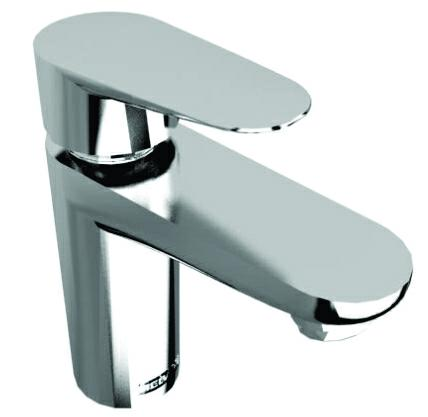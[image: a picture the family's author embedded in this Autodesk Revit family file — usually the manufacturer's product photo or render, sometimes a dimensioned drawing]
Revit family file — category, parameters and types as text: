
# Revit family: Monomando de Lavabo E-928
name_source: partatom
category: Aparatos sanitarios
revit_build: Autodesk Revit 2016 (Build: 20150220_1215(x64)
units: mm (PartAtom-declared; Revit-internal decimal feet)

## family parameters
Compartido = Sí
Corte con vacíos al cargar = No
Cota de conector redondo = Diámetro de uso
Número OmniClass = 23.45.55.14
Punto de cálculo de habitación = Sí
Se basa en plano de trabajo = Sí
Siempre vertical = Sí
Tipo de pieza = Normal
Título OmniClass = Single Faucets

## types (1)
- E-928
    Accesorios = Conectores ½ -14 NPSM
    Altura Total = 6"
    Anchura Total = 2"
    Características del Producto = Monomando tubular para lavabo.
    Cartucho = Cartucho Ø25 mm con vástago metálico.
    Chrome = Brass
    Comentarios de tipo = Monomando tubular para lavabo sin contra.
    Cuerpo de Latón = Brass
    Descripción = Monomando Century E-928
    Elevación por defecto = 1"
    Fabricante = HELVEX S.A. de C.V.
    Garantía = El producto HELVEX está garantizado como libre de defectos en materiales y procesos de fabricación. El producto HELVEX está garantizado, en lo que se refiere a los acabados; por un periodo de 10 años en los acabados cromo y duravex, y por 2 años en acabados diferentes al cromo, a partir de la fecha de compra indicada en la factura.
    Imagen de tipo = E-928.jpg
    Instalación = Conexión ½ - 14 NPSM
    Modelo = E-928
    Operación = El maneral tienen una rotación horizontal para la función de agua caliente y fría; y vertical para abrir y cerrar el flujo de agua.
    Presión Máxima de Trabajo = 85.3 psi
    Presión Mínima de Trabajo = 5.6 psi
    Profundidad Total = 5"
    URL = http://www.helvex.com.mx

## geometry (parser evidence)
native form markers: Sweep x3
no freeform markers — native parametric forms only
